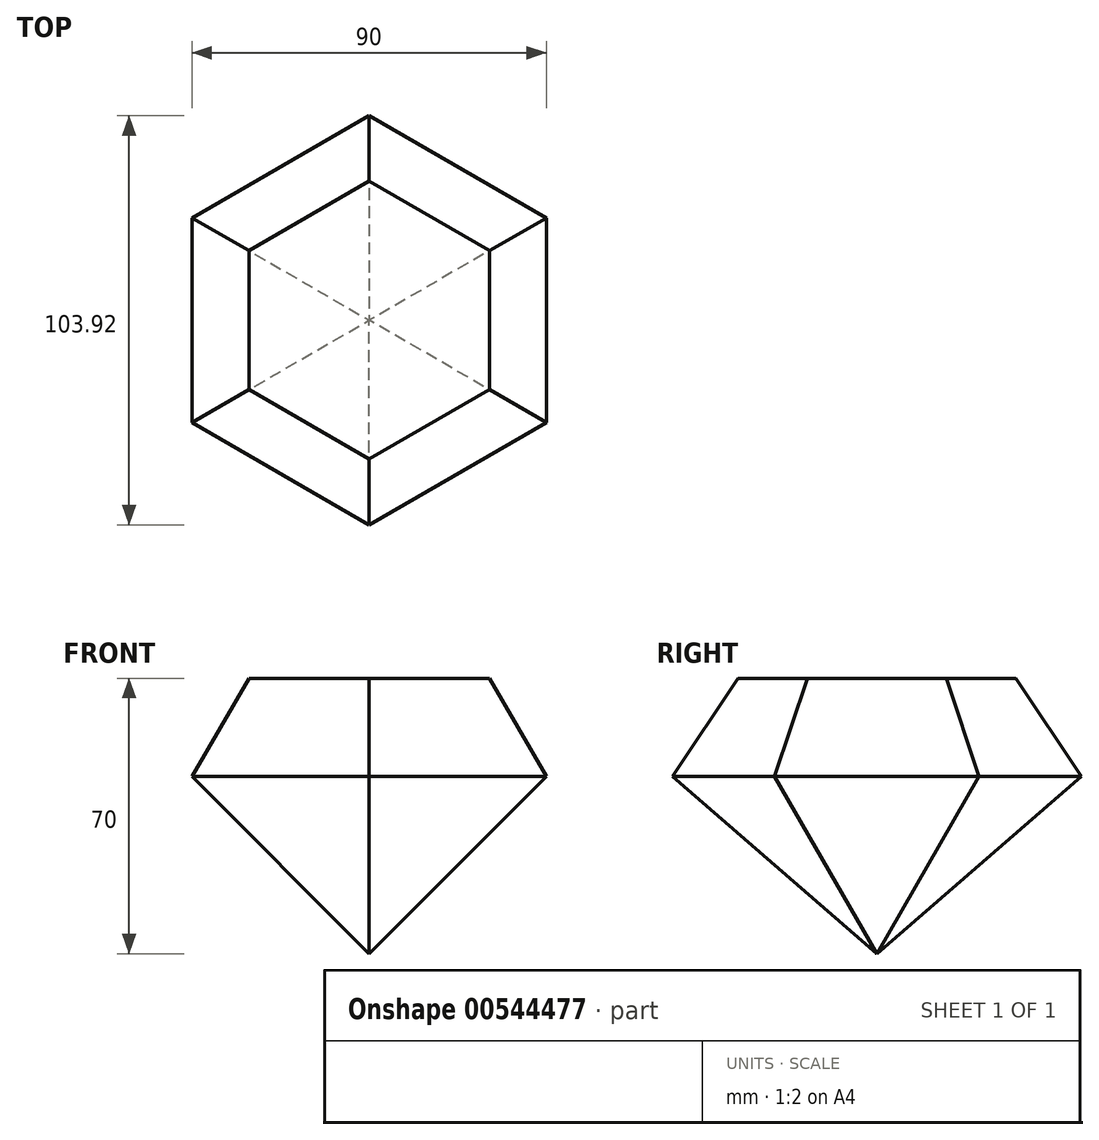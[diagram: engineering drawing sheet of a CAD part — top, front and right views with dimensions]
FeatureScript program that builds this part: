
annotation { "Feature Type Name" : "Feature", "Feature Type Description" : "" }
export const myFeature = defineFeature(function(context is Context, id is Id, definition is map)
    precondition{}
    {
        {
            var Q0;
            Q0=qCreatedBy(makeId("Top.planeOp"),FACE);
            var sketch = newSketch(context, id + "F0", { "sketchPlane" : qUnion([Q0])});
            skCircle(sketch, "E0.cCircle", {"center": v(0, 0) * mm, "radius": 45 * mm, "construction": true});
            skLineSegment(sketch, "E0.0", {"start": v(-45, 25.98) * mm, "end": v(0, 51.96) * mm});
            skLineSegment(sketch, "E0.1", {"start": v(0, 51.96) * mm, "end": v(45, 25.98) * mm});
            skLineSegment(sketch, "E0.2", {"start": v(45, 25.98) * mm, "end": v(45, -25.98) * mm});
            skLineSegment(sketch, "E0.3", {"start": v(45, -25.98) * mm, "end": v(0, -51.96) * mm});
            skLineSegment(sketch, "E0.4", {"start": v(0, -51.96) * mm, "end": v(-45, -25.98) * mm});
            skLineSegment(sketch, "E0.5", {"start": v(-45, -25.98) * mm, "end": v(-45, 25.98) * mm});
            skPoint(sketch, "E0.0.midPoint", {"position": v(-22.5, 38.97) * mm});
            skSolve(sketch);
        }
        {
            var Q0;
            Q0=makeQuery(id+"F0.imprint","IMPRINT",FACE,{"disambiguationData":[TD([[makeQuery(id+"F0.imprint","IMPRINT",EDGE,{"derivedFrom":sQuery(id+"F0.wireOp",EDGE,"E0.0")}),-1.0]])]});
            extrude(context, id + "F1", {"entities" : qUnion([Q0]), "depth" : 25 * mm, "offsetDistance" : 25 * mm, "hasDraft" : true, "draftAngle" : 30 * degree, "draftPullDirection" : true, "hasSecondDirection" : true, "secondDirectionOppositeDirection" : true, "secondDirectionDepth" : 50 * mm, "hasSecondDirectionDraft" : true, "secondDirectionDraftAngle" : 45 * degree, "secondDirectionDraftPullDirection" : true});
        }
    });
